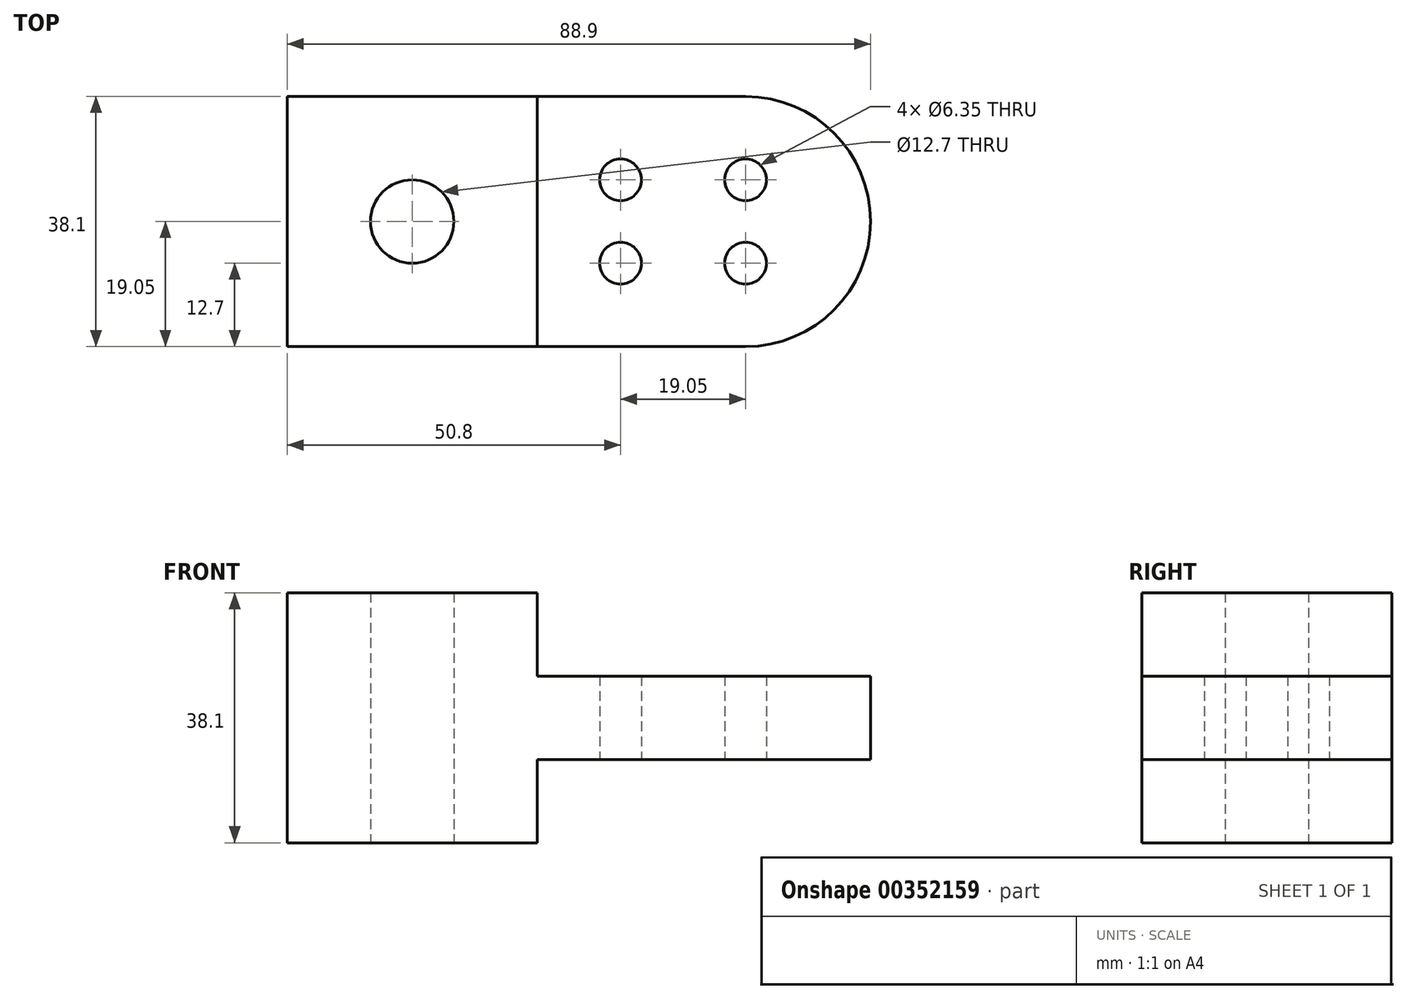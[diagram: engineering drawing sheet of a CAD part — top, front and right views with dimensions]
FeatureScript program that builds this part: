
annotation { "Feature Type Name" : "Feature", "Feature Type Description" : "" }
export const myFeature = defineFeature(function(context is Context, id is Id, definition is map)
    precondition{}
    {
        {
            var Q0;
            Q0=qCreatedBy(makeId("Top.planeOp"),FACE);
            var sketch = newSketch(context, id + "F0", { "sketchPlane" : qUnion([Q0])});
            skLineSegment(sketch, "E0.bottom", {"start": v(-19.05, 19.05) * mm, "end": v(19.05, 19.05) * mm});
            skLineSegment(sketch, "E0.top", {"start": v(-19.05, -19.05) * mm, "end": v(19.05, -19.05) * mm});
            skLineSegment(sketch, "E0.left", {"start": v(-19.05, 19.05) * mm, "end": v(-19.05, -19.05) * mm});
            skLineSegment(sketch, "E0.right", {"start": v(19.05, 19.05) * mm, "end": v(19.05, -19.05) * mm});
            skCircle(sketch, "E1", {"center": v(0, 0) * mm, "radius": 6.35 * mm});
            skSolve(sketch);
        }
        {
            var Q0;
            Q0=makeQuery(id+"F0.imprint","IMPRINT",FACE,{"disambiguationData":[TD([[makeQuery(id+"F0.imprint","IMPRINT",EDGE,{"derivedFrom":sQuery(id+"F0.wireOp",EDGE,"E0.bottom")}),-1.0]])]});
            extrude(context, id + "F1", {"entities" : qUnion([Q0]), "endBound" : BoundingType.SYMMETRIC, "depth" : 38.1 * mm});
        }
        {
            var Q0;
            Q0=qCreatedBy(makeId("Top.planeOp"),FACE);
            var sketch = newSketch(context, id + "F2", { "sketchPlane" : qUnion([Q0])});
            skLineSegment(sketch, "E2", {"start": v(19.05, 19.05) * mm, "end": v(19.05, -19.05) * mm});
            skLineSegment(sketch, "E3", {"start": v(19.05, 19.05) * mm, "end": v(50.8, 19.05) * mm});
            skLineSegment(sketch, "E4", {"start": v(19.05, -19.05) * mm, "end": v(50.8, -19.05) * mm});
            skArc(sketch, "E5", {"start": v(50.8, -19.05) * mm, "mid": v(69.85, 0) * mm, "end": v(50.8, 19.05) * mm});
            skCircle(sketch, "E6", {"center": v(31.75, 6.35) * mm, "radius": 3.18 * mm});
            skCircle(sketch, "E7", {"center": v(50.8, 6.35) * mm, "radius": 3.18 * mm});
            skCircle(sketch, "E8", {"center": v(31.75, -6.35) * mm, "radius": 3.18 * mm});
            skCircle(sketch, "E9", {"center": v(50.8, -6.35) * mm, "radius": 3.18 * mm});
            skSolve(sketch);
        }
        {
            var Q0;
            Q0 = qSketchRegion(id + "F2", true);
            extrude(context, id + "F3", {"entities" : qUnion([Q0]), "operationType" : NewBodyOperationType.ADD, "endBound" : BoundingType.SYMMETRIC, "depth" : 12.7 * mm});
        }
    });
